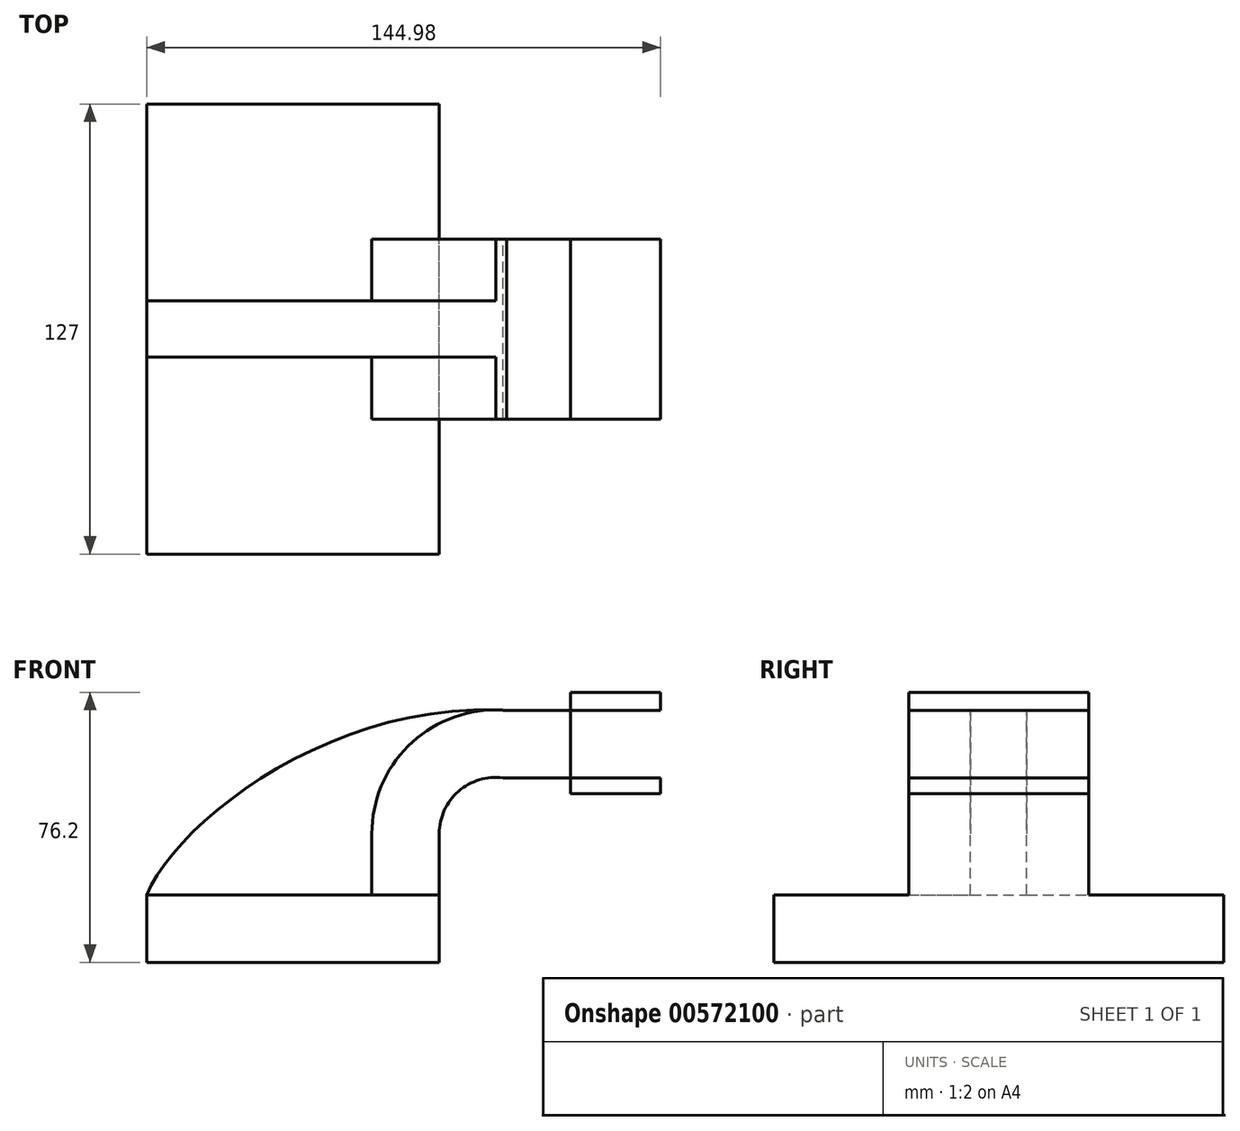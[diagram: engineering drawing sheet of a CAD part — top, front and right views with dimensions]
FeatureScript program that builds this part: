
annotation { "Feature Type Name" : "Feature", "Feature Type Description" : "" }
export const myFeature = defineFeature(function(context is Context, id is Id, definition is map)
    precondition{}
    {
        {
            var Q0;
            Q0=qCreatedBy(makeId("Front.planeOp"),FACE);
            var sketch = newSketch(context, id + "F0", { "sketchPlane" : qUnion([Q0])});
            skLineSegment(sketch, "E0.bottom", {"start": v(-41.28, 9.52) * mm, "end": v(41.28, 9.53) * mm});
            skLineSegment(sketch, "E0.top", {"start": v(-41.28, -9.53) * mm, "end": v(41.28, -9.53) * mm});
            skLineSegment(sketch, "E0.left", {"start": v(-41.28, 9.52) * mm, "end": v(-41.28, -9.53) * mm});
            skLineSegment(sketch, "E0.right", {"start": v(41.28, 9.53) * mm, "end": v(41.28, -9.52) * mm});
            skPoint(sketch, "E0.middle", {"position": v(0, 0) * mm});
            skLineSegment(sketch, "E1", {"start": v(41.27, 9.53) * mm, "end": v(41.27, 26.76) * mm});
            skLineSegment(sketch, "E2.bottom", {"start": v(129.1, 38.1) * mm, "end": v(78.3, 38.1) * mm});
            skLineSegment(sketch, "E2.top", {"start": v(129.1, 66.67) * mm, "end": v(78.3, 66.67) * mm});
            skLineSegment(sketch, "E2.left", {"start": v(129.1, 38.1) * mm, "end": v(129.1, 66.68) * mm});
            skLineSegment(sketch, "E2.right", {"start": v(78.3, 38.1) * mm, "end": v(78.3, 66.68) * mm});
            skPoint(sketch, "E2.middle", {"position": v(103.7, 52.39) * mm});
            skLineSegment(sketch, "E3", {"start": v(78.3, 42.5) * mm, "end": v(59.25, 42.5) * mm});
            skArc(sketch, "E4", {"start": v(59.25, 42.5) * mm, "mid": v(46.7, 38.7) * mm, "end": v(41.27, 26.76) * mm});
            skLineSegment(sketch, "E5.0", {"start": v(22.22, 9.53) * mm, "end": v(22.22, 26.76) * mm});
            skArc(sketch, "E5.1", {"start": v(60.28, 61.54) * mm, "mid": v(33.59, 52.53) * mm, "end": v(22.22, 26.76) * mm});
            skLineSegment(sketch, "E5.2", {"start": v(78.44, 61.54) * mm, "end": v(60.28, 61.54) * mm});
            skFitSpline(sketch, "E6", {"points": [v(-41.28, 9.52) * mm, v(60.28, 61.54) * mm], "startDerivative": vector(25.52, 61.95) * mm, "endDerivative": vector(147.66, -9.08) * mm});
            skLineSegment(sketch, "E7", {"start": v(103.7, 52.39) * mm, "end": v(103.7, 66.68) * mm});
            skLineSegment(sketch, "E8", {"start": v(103.7, 52.39) * mm, "end": v(103.7, 38.1) * mm});
            skLineSegment(sketch, "E9", {"start": v(78.44, 61.54) * mm, "end": v(103.7, 61.54) * mm});
            skLineSegment(sketch, "E10", {"start": v(78.3, 42.5) * mm, "end": v(103.7, 42.5) * mm});
            skSolve(sketch);
        }
        {
            var Q0;
            Q0=makeQuery(id+"F0.imprint","IMPRINT",FACE,{"disambiguationData":[TD([[makeQuery(id+"F0.imprint","IMPRINT",EDGE,{"derivedFrom":sQuery(id+"F0.wireOp",EDGE,"E0.top")}),1.0]])]});
            extrude(context, id + "F1", {"entities" : qUnion([Q0]), "endBound" : BoundingType.SYMMETRIC, "depth" : 127 * mm, "offsetDistance" : 25.4 * mm});
        }
        {
            var Q0;
            {var subQ3=sQuery(id+"F0.wireOp",EDGE,"E1");Q0=makeQuery(id+"F0.imprint","IMPRINT",FACE,{"disambiguationData":[TD([[makeQuery(id+"F0.imprint","IMPRINT",EDGE,{"derivedFrom":subQ3}),1.0]])]});}
            var Q1;
            {var subQ1=sQuery(id+"F0.wireOp",EDGE,"E2.bottom");Q1=makeQuery(id+"F0.imprint","IMPRINT",FACE,{"disambiguationData":[TD([[makeQuery(id+"F0.imprint","IMPRINT",EDGE,{"derivedFrom":subQ1}),-1.0]])]});}
            var Q2;
            {var subQ7=sQuery(id+"F0.wireOp",EDGE,"E7");Q2=makeQuery(id+"F0.imprint","IMPRINT",FACE,{"disambiguationData":[TD([[makeQuery(id+"F0.imprint","IMPRINT",EDGE,{"derivedFrom":subQ7}),1.0]])]});}
            extrude(context, id + "F2", {"entities" : qUnion([Q0, Q1, Q2]), "operationType" : NewBodyOperationType.ADD, "endBound" : BoundingType.SYMMETRIC, "depth" : 50.8 * mm, "offsetDistance" : 25.4 * mm});
        }
        {
            var Q0;
            {var subQ3=sQuery(id+"F0.wireOp",EDGE,"E5.0");Q0=makeQuery(id+"F0.imprint","IMPRINT",FACE,{"disambiguationData":[TD([[makeQuery(id+"F0.imprint","IMPRINT",EDGE,{"derivedFrom":subQ3}),1.0]])]});}
            extrude(context, id + "F3", {"entities" : qUnion([Q0]), "operationType" : NewBodyOperationType.ADD, "endBound" : BoundingType.SYMMETRIC, "depth" : 15.88 * mm, "offsetDistance" : 25.4 * mm});
        }
    });
